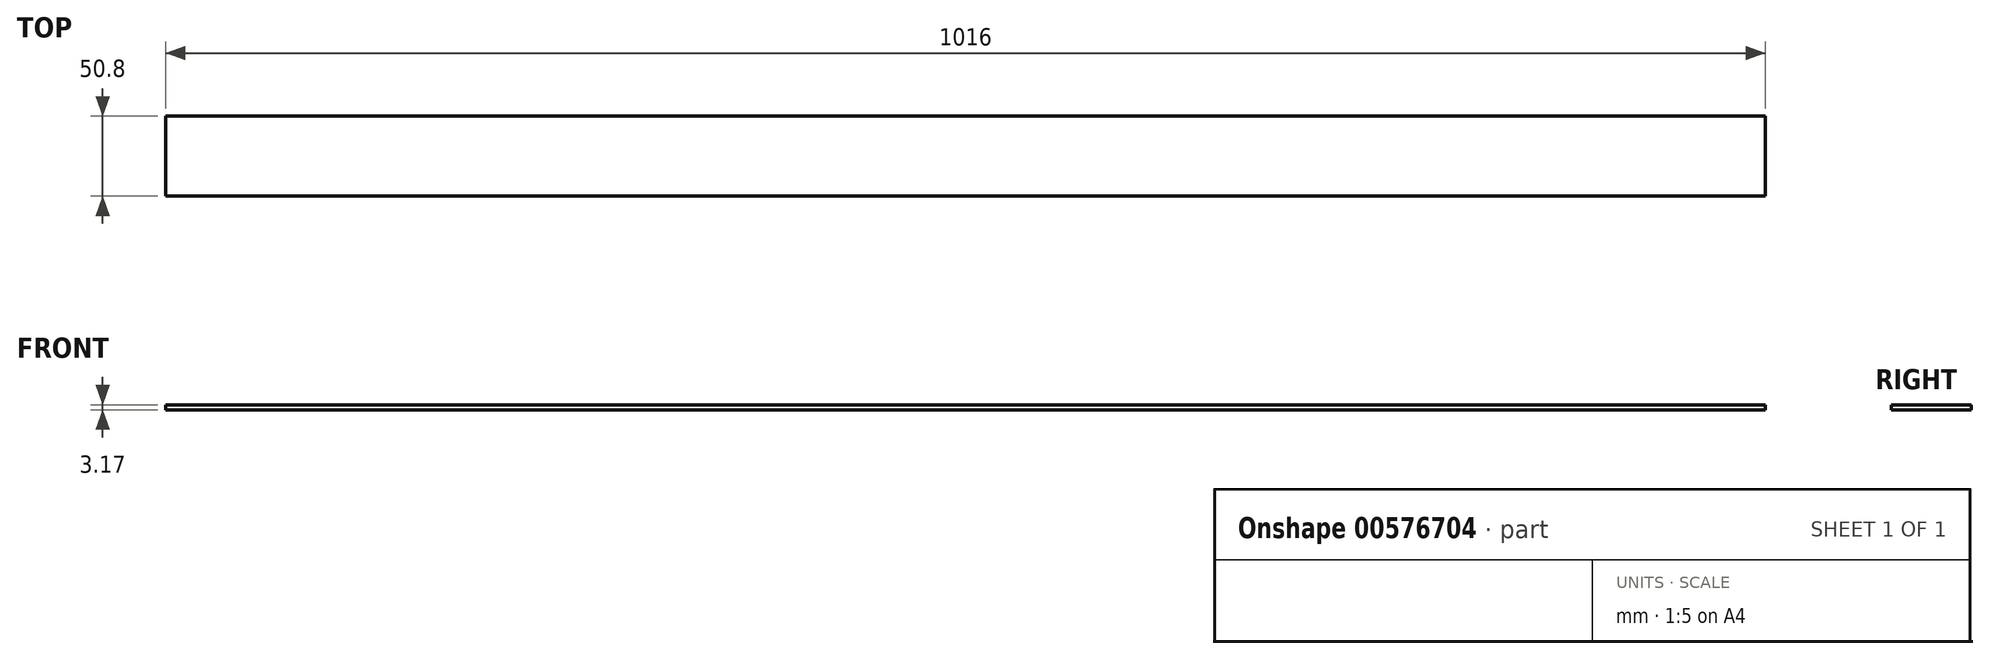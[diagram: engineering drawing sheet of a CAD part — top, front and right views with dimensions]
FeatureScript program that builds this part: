
annotation { "Feature Type Name" : "Feature", "Feature Type Description" : "" }
export const myFeature = defineFeature(function(context is Context, id is Id, definition is map)
    precondition{}
    {
        {
            var Q0;
            Q0=qCreatedBy(makeId("Top.planeOp"),FACE);
            var sketch = newSketch(context, id + "F0", { "sketchPlane" : qUnion([Q0])});
            skLineSegment(sketch, "E0.bottom", {"start": v(508, 25.4) * mm, "end": v(-508, 25.4) * mm});
            skLineSegment(sketch, "E0.top", {"start": v(508, -25.4) * mm, "end": v(-508, -25.4) * mm});
            skLineSegment(sketch, "E0.left", {"start": v(508, 25.4) * mm, "end": v(508, -25.4) * mm});
            skLineSegment(sketch, "E0.right", {"start": v(-508, 25.4) * mm, "end": v(-508, -25.4) * mm});
            skPoint(sketch, "E0.middle", {"position": v(0, 0) * mm});
            skLineSegment(sketch, "E1", {"start": v(-558.8, 25.4) * mm, "end": v(-508, -25.4) * mm});
            skLineSegment(sketch, "E2", {"start": v(558.8, 25.4) * mm, "end": v(508, -25.4) * mm});
            skSolve(sketch);
        }
        {
            var Q0;
            Q0 = qSketchRegion(id + "F0", true);
            extrude(context, id + "F1", {"entities" : qUnion([Q0]), "depth" : 3.17 * mm, "offsetDistance" : 25.4 * mm});
        }
    });
